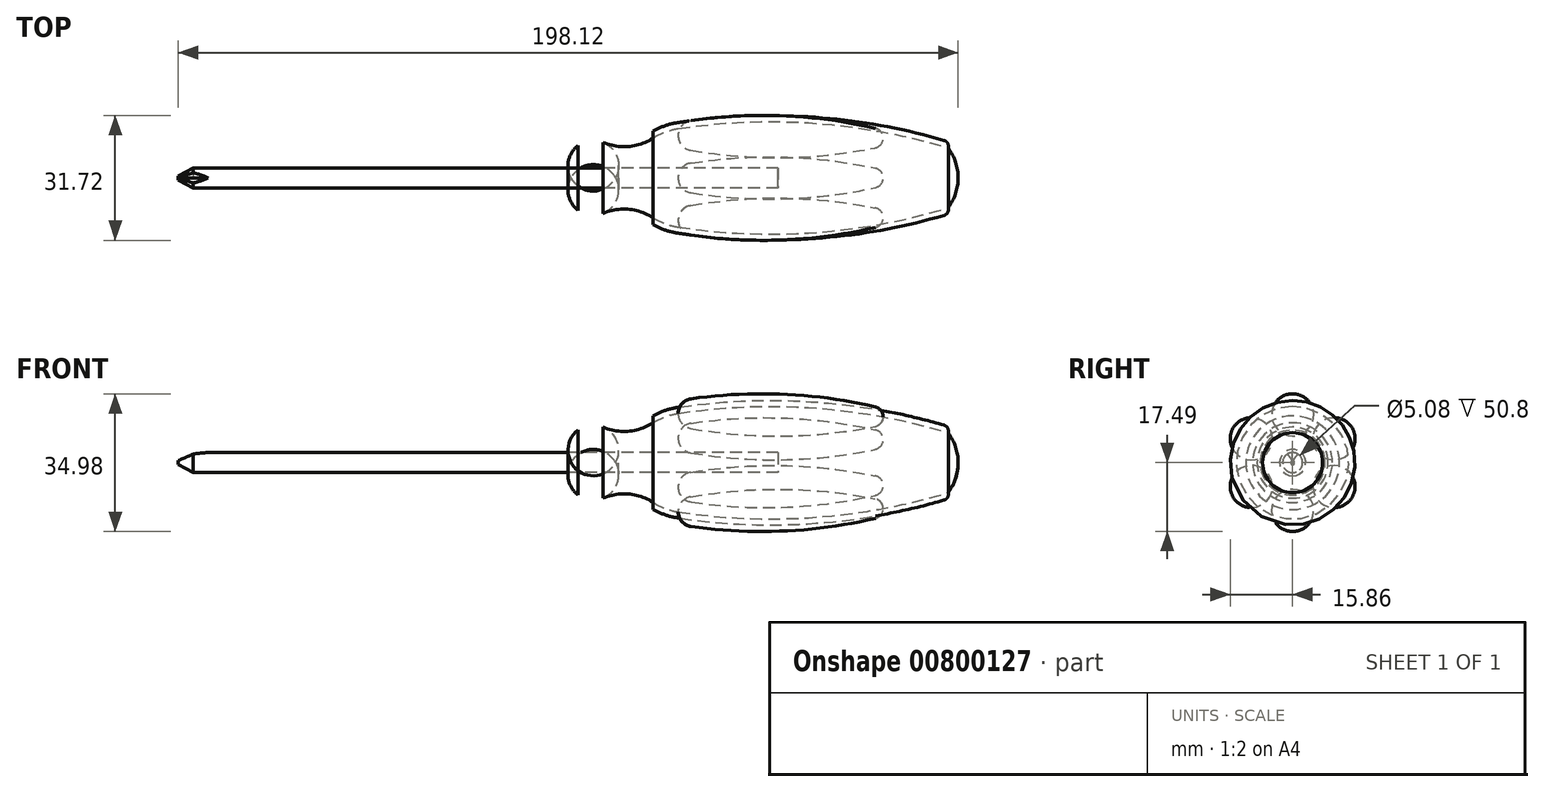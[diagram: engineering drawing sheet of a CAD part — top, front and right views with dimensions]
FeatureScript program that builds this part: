
annotation { "Feature Type Name" : "Feature", "Feature Type Description" : "" }
export const myFeature = defineFeature(function(context is Context, id is Id, definition is map)
    precondition{}
    {
        {
            var Q0;
            Q0=qCreatedBy(makeId("Front.planeOp"),FACE);
            var sketch = newSketch(context, id + "F0", { "sketchPlane" : qUnion([Q0])});
            skLineSegment(sketch, "E0", {"start": v(-101.6, 0) * mm, "end": v(96.52, 0) * mm});
            skLineSegment(sketch, "E1", {"start": v(96.52, 0) * mm, "end": v(117.55, 0) * mm, "construction": true});
            skLineSegment(sketch, "E2", {"start": v(50.8, 2.54) * mm, "end": v(-97.8, 2.54) * mm});
            skLineSegment(sketch, "E3", {"start": v(-101.6, 0.5) * mm, "end": v(-101.6, 0) * mm});
            skLineSegment(sketch, "E4", {"start": v(0, 2.54) * mm, "end": v(0, 8.25) * mm});
            skArc(sketch, "E5", {"start": v(6.35, 9.02) * mm, "mid": v(3.07, 9.48) * mm, "end": v(0, 8.25) * mm});
            skArc(sketch, "E6", {"start": v(6.35, 9.02) * mm, "mid": v(12.84, 7.99) * mm, "end": v(19.05, 10.11) * mm});
            skArc(sketch, "E7", {"start": v(25.4, 12.52) * mm, "mid": v(22.1, 11.65) * mm, "end": v(19.05, 10.11) * mm});
            skArc(sketch, "E8", {"start": v(93.98, 7.62) * mm, "mid": v(59.96, 13.9) * mm, "end": v(25.4, 12.52) * mm});
            skArc(sketch, "E9", {"start": v(96.52, 0) * mm, "mid": v(95.87, 4.02) * mm, "end": v(93.98, 7.62) * mm});
            skArc(sketch, "E10.0", {"start": v(25.17, 14.02) * mm, "mid": v(22.01, 13.24) * mm, "end": v(19.05, 11.9) * mm});
            skArc(sketch, "E10.1", {"start": v(92.95, 9.52) * mm, "mid": v(59.3, 15.46) * mm, "end": v(25.17, 14.02) * mm});
            skLineSegment(sketch, "E11", {"start": v(19.05, 11.9) * mm, "end": v(19.05, 10.11) * mm});
            skArc(sketch, "E12", {"start": v(93.98, 7.62) * mm, "mid": v(93.86, 8.78) * mm, "end": v(92.95, 9.52) * mm});
            skPoint(sketch, "E13.orphan", {"position": v(0, 0) * mm});
            skLineSegment(sketch, "E14", {"start": v(50.8, 2.54) * mm, "end": v(50.8, 0) * mm});
            skLineSegment(sketch, "E15", {"start": v(-101.6, 0.5) * mm, "end": v(-97.8, 2.54) * mm});
            skPoint(sketch, "E16.orphan", {"position": v(-101.6, 2.54) * mm});
            skSolve(sketch);
        }
        {
            var Q0;
            Q0=qCreatedBy(makeId("Front.planeOp"),FACE);
            var sketch = newSketch(context, id + "F1", { "sketchPlane" : qUnion([Q0])});
            skLineSegment(sketch, "E17", {"start": v(25.4, 12.52) * mm, "end": v(77.47, 11.64) * mm});
            skArc(sketch, "E18", {"start": v(28.67, 16.22) * mm, "mid": v(26.35, 14.97) * mm, "end": v(25.4, 12.52) * mm});
            skArc(sketch, "E19", {"start": v(77.47, 11.64) * mm, "mid": v(76.93, 13.25) * mm, "end": v(75.5, 14.16) * mm});
            skArc(sketch, "E20", {"start": v(75.5, 14.16) * mm, "mid": v(52.19, 17.37) * mm, "end": v(28.67, 16.22) * mm});
            skSolve(sketch);
        }
        {
            var Q0;
            Q0=qCreatedBy(makeId("Front.planeOp"),FACE);
            var sketch = newSketch(context, id + "F2", { "sketchPlane" : qUnion([Q0])});
            skLineSegment(sketch, "E21", {"start": v(-101.6, 0.5) * mm, "end": v(-93.98, 2.54) * mm});
            skSolve(sketch);
        }
        {
            var Q0;
            Q0=sQuery(id+"F2.wireOp",VERTEX,"E21.start");
            var Q1;
            Q1=sQuery(id+"F2.wireOp",EDGE,"E21");
            cPlane(context, id + "F3", {"entities" : qUnion([Q0, Q1]), "cplaneType" : CPlaneType.LINE_POINT, "offset" : 25.4 * mm, "width" : 152.4 * mm, "height" : 152.4 * mm});
        }
        {
            var Q0;
            Q0=qCreatedBy(id+"F3.planeOp",FACE);
            var sketch = newSketch(context, id + "F4", { "sketchPlane" : qUnion([Q0])});
            skLineSegment(sketch, "E22", {"start": v(5.08, 29.2) * mm, "end": v(0, 26.67) * mm});
            skLineSegment(sketch, "E23", {"start": v(0, 26.67) * mm, "end": v(-5.08, 29.2) * mm});
            skLineSegment(sketch, "E24", {"start": v(-5.08, 29.2) * mm, "end": v(5.08, 29.2) * mm});
            skLineSegment(sketch, "E25", {"start": v(0, 29.2) * mm, "end": v(0, 26.67) * mm, "construction": true});
            skSolve(sketch);
        }
        {
            var Q0;
            {var subQ0=sQuery(id+"F0.wireOp",EDGE,"E3");Q0=makeQuery(id+"F0.imprint","IMPRINT",FACE,{"disambiguationData":[TD([[makeQuery(id+"F0.imprint","IMPRINT",EDGE,{"derivedFrom":subQ0}),1.0]])]});}
            var Q1;
            Q1=sQuery(id+"F0.wireOp",EDGE,"E1");
            revolve(context, id + "F5", {"entities" : qUnion([Q0]), "axis" : qUnion([Q1]), "revolveType" : RevolveType.FULL, "surfaceOperationType" : NewSurfaceOperationType.NEW});
        }
        {
            var Q0;
            {var subQ0=sQuery(id+"F0.wireOp",EDGE,"E4");Q0=makeQuery(id+"F0.imprint","IMPRINT",FACE,{"disambiguationData":[TD([[makeQuery(id+"F0.imprint","IMPRINT",EDGE,{"derivedFrom":subQ0}),-1.0]])]});}
            var Q1;
            Q1=sQuery(id+"F0.wireOp",EDGE,"E1");
            revolve(context, id + "F6", {"entities" : qUnion([Q0]), "axis" : qUnion([Q1]), "revolveType" : RevolveType.FULL, "surfaceOperationType" : NewSurfaceOperationType.NEW});
        }
        {
            var Q0;
            Q0=makeQuery(id+"F0.imprint","IMPRINT",FACE,{"disambiguationData":[TD([[makeQuery(id+"F0.imprint","IMPRINT",EDGE,{"derivedFrom":sQuery(id+"F0.wireOp",EDGE,"E7")}),-1.0]])]});
            var Q1;
            Q1=sQuery(id+"F0.wireOp",EDGE,"E1");
            revolve(context, id + "F7", {"entities" : qUnion([Q0]), "axis" : qUnion([Q1]), "revolveType" : RevolveType.FULL, "surfaceOperationType" : NewSurfaceOperationType.NEW});
        }
        {
            var Q0;
            Q0=makeQuery(id+"F1.imprint","IMPRINT",FACE,{"disambiguationData":[TD([[makeQuery(id+"F1.imprint","IMPRINT",EDGE,{"derivedFrom":sQuery(id+"F1.wireOp",EDGE,"E17")}),1.0]])]});
            var Q1;
            Q1=sQuery(id+"F1.wireOp",EDGE,"E17");
            revolve(context, id + "F8", {"entities" : qUnion([Q0]), "axis" : qUnion([Q1]), "revolveType" : RevolveType.FULL, "surfaceOperationType" : NewSurfaceOperationType.NEW});
        }
        {
            var Q0;
            Q0=makeQuery(id+"F8.opRevolve","SWEPT_BODY",BODY,{"disambiguationData":[OSD([sQuery(id+"F1.wireOp",EDGE,"E17"),sQuery(id+"F1.wireOp",EDGE,"E18"),sQuery(id+"F1.wireOp",EDGE,"E19"),sQuery(id+"F1.wireOp",EDGE,"E20")])]});
            var Q1;
            Q1=sQuery(id+"F0.wireOp",EDGE,"E1");
            circularPattern(context, id + "F9", {"entities" : qUnion([Q0]), "axis" : qUnion([Q1]), "angle" : 360 * degree, "instanceCount" : 6, "equalSpace" : true});
        }
        {
            var Q0;
            Q0=makeQuery(id+"F6.opRevolve","SWEPT_BODY",BODY,{"disambiguationData":[OSD([sQuery(id+"F0.wireOp",EDGE,"E0"),sQuery(id+"F0.wireOp",EDGE,"E2"),sQuery(id+"F0.wireOp",EDGE,"E4"),sQuery(id+"F0.wireOp",EDGE,"E5"),sQuery(id+"F0.wireOp",EDGE,"E6"),sQuery(id+"F0.wireOp",EDGE,"E7"),sQuery(id+"F0.wireOp",EDGE,"E8"),sQuery(id+"F0.wireOp",EDGE,"E9"),sQuery(id+"F0.wireOp",EDGE,"E14")])]});
            var Q1;
            Q1=makeQuery(id+"F7.opRevolve","SWEPT_BODY",BODY,{"disambiguationData":[OSD([sQuery(id+"F0.wireOp",EDGE,"E7"),sQuery(id+"F0.wireOp",EDGE,"E8"),sQuery(id+"F0.wireOp",EDGE,"E10.0"),sQuery(id+"F0.wireOp",EDGE,"E10.1"),sQuery(id+"F0.wireOp",EDGE,"E11"),sQuery(id+"F0.wireOp",EDGE,"E12")])]});
            booleanBodies(context, id + "F10", {"operationType" : BooleanOperationType.SUBTRACTION, "tools" : qUnion([Q0]), "targets" : qUnion([Q1]), "keepTools" : true});
        }
        {
            var Q0;
            Q0=qSketchRegion(id+"F4",true);
            var Q1;
            Q1=qConstructionFilter(qBodyType(qCreatedBy(id+"F2",EDGE),BodyType.WIRE),ConstructionObject.NO);
            sweep(context, id + "F11", {"operationType" : NewBodyOperationType.REMOVE, "profiles" : qUnion([Q0]), "path" : qUnion([Q1])});
        }
    });
